# Revit family: Z-R1414
name_source: partatom
category: Plumbing Fixtures
revit_build: Autodesk Revit 2018 (Build: 20170223_1515(x64)
units: mm (PartAtom-declared; Revit-internal decimal feet)

## family parameters
Cut with Voids When Loaded = Yes
Host = Face
OmniClass Number = 23.65.35.11.14
OmniClass Title = Instantaneous Water Heaters
Part Type = Normal
Room Calculation Point = No
Round Connector Dimension = Use Diameter
Shared = Yes

## types (15) — shared parameters
ADA Compliant = Yes
AKL-Allen Key Latch = No
Assembly Code = D2020200
Body Material = Plastic-Chronomite-Celcon
CL-Cylinder Lock (one per door = No
CW Connection = No
Chassis And Door Material = Metal-Chronomite-Steel_Galvannealed
Cold Water Connection Diameter = 3/4"
Cold Water Connection Radius = 3/8"
Country = U.S.A.
Default Elevation = 0"
Description = Wall Sleeve for R Tankless Heaters
Flow Rate = 0.65 GPM to 5.0 GPM (2.5 LPM to 18.9 LPM)
HW Connection = No
Height = 9 7/8"
Hot Water Connection Diameter = 3/4"
Hot Water Connection Radius = 3/8"
Housing Depth = 5 1/4"
Housing Description = Vandal resistant rugged cast aluminum housing
Housing Side Inner Dimension = 14"
Housing Side Outer Dimension = 15 5/8"
IAPMO Compliance = Meets applicable building codes including ADA, UL, IAPMO, UPC and CS
Installation Type = Wall Mounted
Length = 10 5/8"
Manufacturer = Chronomite
Maximum Ambient Operating Temperature = 140°F
Maximum Operating Pressure = 80PSI
Maximum Pressure = 150 PSI
Maximum Water Temperature = 160°F
Minimum Flow Rate = 1 GPM
Minimum Operating Pressure = 25 PSI
Model = Z-R1414
Price = Prices may vary. Please consult Manufacturer Representative for most up-to-date price list.
Product Documentation Link = https://www.chronomite.com
Product Page URL = https://www.chronomite.com
SS-Stainless Steel Construction  m(Type 304 No. 4 Satin Finish = No
Shipping Weight = 10 lbs.
URL = www.chronomite.com
Vent Connection = No
Waste Connection = No
Width = 4 1/4"
zero-valued in all types: CWFU, HWFU, WFU

## per-type parameters (varying)
| type | Electric Potential | Electrical Current | Power | Temperature Rise @ 1.5 GPM | Temperature Rise @ 2.5 GPM | Temperature Rise @ 3 GPM |
| R-48S/208 | 208 V | 48 A | 10000 W | 45 °F | 27 °F | 23 °F |
| R-48S/240 | 240 V | 48 A | 11500 W | 52 °F | 31 °F | 26 °F |
| R-58S/208 | 208 V | 58 A | 12050 W | 55 °F | 33 °F | 27 °F |
| R-63S/208 | 208 V | 63 A | 13100 W | 60 °F | 36 °F | 30 °F |
| R-48S/277 | 277 V | 48 A | 13300 W | 61 °F | 36 °F | 30 °F |
| R-58S/240 | 240 V | 58 A | 13900 W | 63 °F | 38 °F | 32 °F |
| R-68S/208 | 208 V | 68 A | 14150 W | 64 °F | 39 °F | 32 °F |
| R-63S/240 | 240 V | 63 A | 15100 W | 69 °F | 41 °F | 34 °F |
| R-75S/208 | 208 V | 75 A | 15600 W | 71 °F | 43 °F | 36 °F |
| R-58S/277 | 277 V | 58 A | 16050 W | 73 °F | 44 °F | 37 °F |
| R-68S/240 | 240 V | 68 A | 16300 W | 74 °F | 45 °F | 37 °F |
| R-63S/277 | 277 V | 63 A | 17450 W | 79 °F | 48 °F | 40 °F |
| R-75S/240 | 240 V | 75 A | 18000 W | 82 °F | 49 °F | 41 °F |
| R-68S/277 | 277 V | 68 A | 18850 W | 86 °F | 51 °F | 43 °F |
| R-75S/277 | 277 V | 75 A | 20750 W | 95 °F | 57 °F | 47 °F |

## geometry (parser evidence)
native form markers: Sweep x3
no freeform markers — native parametric forms only
